# Revit family: d0087280_REVIT-TCX-DUAL
name_source: partatom
category: Mechanical Equipment
revit_build: Autodesk Revit 2017 (Build: 20190507_1515(x64)
units: mm (PartAtom-declared; Revit-internal decimal feet)

## family parameters
Always vertical = Yes
Cut with Voids When Loaded = No
Part Type = Normal
Room Calculation Point = No
Round Connector Dimension = Use Radius
Shared = No
Work Plane-Based = No

## types (44) — shared parameters
Assembly Code = D3040400
Clean in Place Connection NPT = 3/4"
Clean in Place Connection Radius = 3/8"
Controll Access Angle = 45.00°
Description = AquaPLEX® Storage Tank (unlined duplex alloy) with COBREX® Steam Heat Exchanger - Double-wall
Disclaimer = This rendering is for building modeling purposes only. Submittal/catalog is still the contract document. PVI reserves the right to change design and specification without notice.
Drain Angle = 90.00°
Enclosure Height = 16"
Enclosure Width = 8"
From Heater Radius = 1 1/2"
Header Location = 10"
Manufacturer = PVI Industries, LLC
Manway Access Radius = 6 1/2"
Relief NPT = 1"
Relief Radius = 1/2"
Safety Relief Valve NPT = 1"
Safety Relief Valve Radius = 1/2"
Steam Supply Flanged = 3"
To Heater Radius = 1 1/2"
URL = www.pvi.com

## per-type parameters (varying)
- 1200-2 L 250A-TCX: Amps @ 120V=6 A; Cold Inlet Extension=24"; Cold Inlet Height=17 7/8"; Cold Inlet NPT=2"; Cold Inlet Radius=1"; Condensate Connection NPT=1 1/4"; Condensate Connection Radius=5/8"; Drain Extension=26 7/8"; Drain Height=3 1/2"; Drain NPT=1"; Drain Radius=1/2"; Enclosure Extension=30"; Flat Side Distance=45 255/256"; From Heater Extension=24"; From Heater Height=19"; Gallons Storage=250 CF; Height to Enclosure=40"; Hot Outlet NPT=2"; Hot Outlet Radius=1"; Manway Access Extension=26"; Relief Angle=45.00°; Relief Extension=27"; Relief Height=46 1/4"; Skid Length=46"; Skid Spacing=27"; Skid Width Between Centers=31"; TCX=TCX : 1200 150-400; Tank Location=44 77/128"; To Heater Extension=24"; To Heater Height=27"; Unit Diameter=46"; Unit Height=63"; Unit Radius=23"
- 1200-2 L 750A-TCX: Amps @ 120V=6 A; Cold Inlet Extension=34 1/2"; Cold Inlet Height=22 1/2"; Cold Inlet NPT=3"; Cold Inlet Radius=1 1/2"; Condensate Connection NPT=1 1/4"; Condensate Connection Radius=5/8"; Drain Extension=37 3/8"; Drain Height=3 3/4"; Drain NPT=1 1/2"; Drain Radius=3/4"; Enclosure Extension=40 1/2"; Flat Side Distance=66 255/256"; From Heater Extension=34 1/2"; From Heater Height=23"; Gallons Storage=750 CF; Height to Enclosure=54"; Hot Outlet NPT=3"; Hot Outlet Radius=1 1/2"; Manway Access Extension=36 1/2"; Relief Angle=45.00°; Relief Extension=37 1/2"; Relief Height=62 1/4"; Skid Length=68"; Skid Spacing=36"; Skid Width Between Centers=40"; TCX=TCX : 1200 500-1000; Tank Location=55 161/256"; To Heater Extension=34 1/2"; To Heater Height=31"; Unit Diameter=67"; Unit Height=83"; Unit Radius=33 1/2"
- 1200-2 L 900A-TCX: Amps @ 120V=6 A; Cold Inlet Extension=34 1/2"; Cold Inlet Height=22 1/2"; Cold Inlet NPT=3"; Cold Inlet Radius=1 1/2"; Condensate Connection NPT=1 1/4"; Condensate Connection Radius=5/8"; Drain Extension=37 3/8"; Drain Height=3 3/4"; Drain NPT=1 1/2"; Drain Radius=3/4"; Enclosure Extension=40 1/2"; Flat Side Distance=66 255/256"; From Heater Extension=34 1/2"; From Heater Height=23"; Gallons Storage=900 CF; Height to Enclosure=54"; Hot Outlet NPT=3"; Hot Outlet Radius=1 1/2"; Manway Access Extension=36 1/2"; Relief Angle=45.00°; Relief Extension=37 1/2"; Relief Height=74 1/4"; Skid Length=68"; Skid Spacing=36"; Skid Width Between Centers=40"; TCX=TCX : 1200 500-1000; Tank Location=55 161/256"; To Heater Extension=34 1/2"; To Heater Height=31"; Unit Diameter=67"; Unit Height=95"; Unit Radius=33 1/2"
- 1200-2 L 1000A-TCX: Amps @ 120V=6 A; Cold Inlet Extension=34 1/2"; Cold Inlet Height=22 1/2"; Cold Inlet NPT=3"; Cold Inlet Radius=1 1/2"; Condensate Connection NPT=1 1/4"; Condensate Connection Radius=5/8"; Drain Extension=37 3/8"; Drain Height=3 3/4"; Drain NPT=1 1/2"; Drain Radius=3/4"; Enclosure Extension=40 1/2"; Flat Side Distance=66 255/256"; From Heater Extension=34 1/2"; From Heater Height=23"; Gallons Storage=1000 CF; Height to Enclosure=54"; Hot Outlet NPT=3"; Hot Outlet Radius=1 1/2"; Manway Access Extension=36 1/2"; Relief Angle=45.00°; Relief Extension=37 1/2"; Relief Height=86 1/4"; Skid Length=68"; Skid Spacing=36"; Skid Width Between Centers=40"; TCX=TCX : 1200 500-1000; Tank Location=55 161/256"; To Heater Extension=34 1/2"; To Heater Height=31"; Unit Diameter=67"; Unit Height=107"; Unit Radius=33 1/2"
- 1200-2 L 175A-TCX: Amps @ 120V=6 A; Cold Inlet Extension=19 1/2"; Cold Inlet Height=15 3/4"; Cold Inlet NPT=2"; Cold Inlet Radius=1"; Condensate Connection NPT=1 1/4"; Condensate Connection Radius=5/8"; Drain Extension=22 3/8"; Drain Height=3 1/2"; Drain NPT=1"; Drain Radius=1/2"; Enclosure Extension=25 1/2"; Flat Side Distance=34"; From Heater Extension=19 1/2"; From Heater Height=19"; Gallons Storage=175 CF; Height to Enclosure=44"; Hot Outlet NPT=2"; Hot Outlet Radius=1"; Manway Access Extension=1"; Relief Angle=38.00°; Relief Extension=22 1/2"; Relief Height=59 1/4"; Skid Length=37"; Skid Spacing=17"; Skid Width Between Centers=21"; TCX=TCX : 1200 150-400; Tank Location=41 1/4"; To Heater Extension=19 1/2"; To Heater Height=27"; Unit Diameter=37"; Unit Height=71"; Unit Radius=18 1/2"
- 1200-2 L 215A-TCX: Amps @ 120V=6 A; Cold Inlet Extension=19 1/2"; Cold Inlet Height=15 3/4"; Cold Inlet NPT=2"; Cold Inlet Radius=1"; Condensate Connection NPT=1 1/4"; Condensate Connection Radius=5/8"; Drain Extension=22 3/8"; Drain Height=3 1/2"; Drain NPT=1"; Drain Radius=1/2"; Enclosure Extension=25 1/2"; Flat Side Distance=34"; From Heater Extension=19 1/2"; From Heater Height=19"; Gallons Storage=215 CF; Height to Enclosure=54"; Hot Outlet NPT=2"; Hot Outlet Radius=1"; Manway Access Extension=1"; Relief Angle=38.00°; Relief Extension=22 1/2"; Relief Height=66 1/4"; Skid Length=37"; Skid Spacing=17"; Skid Width Between Centers=21"; TCX=TCX : 1200 150-400; Tank Location=41 1/4"; To Heater Extension=19 1/2"; To Heater Height=27"; Unit Diameter=37"; Unit Height=78"; Unit Radius=18 1/2"
- 1800-2 L 150A-TCX: Amps @ 120V=6 A; Cold Inlet Extension=19 1/2"; Cold Inlet Height=15 3/4"; Cold Inlet NPT=2"; Cold Inlet Radius=1"; Condensate Connection NPT=1 1/2"; Condensate Connection Radius=3/4"; Drain Extension=22 3/8"; Drain Height=3 1/2"; Drain NPT=1"; Drain Radius=1/2"; Enclosure Extension=25 1/2"; Flat Side Distance=34"; From Heater Extension=19 1/2"; From Heater Height=19"; Gallons Storage=150 CF; Height to Enclosure=40"; Hot Outlet NPT=2"; Hot Outlet Radius=1"; Manway Access Extension=1"; Relief Angle=38.00°; Relief Extension=22 1/2"; Relief Height=53 1/4"; Skid Length=37"; Skid Spacing=17"; Skid Width Between Centers=21"; TCX=TCX : 1800 150-400; Tank Location=41 1/4"; To Heater Extension=19 1/2"; To Heater Height=27"; Unit Diameter=37"; Unit Height=65"; Unit Radius=18 1/2"
- 1800-2 L 175A-TCX: Amps @ 120V=6 A; Cold Inlet Extension=19 1/2"; Cold Inlet Height=15 3/4"; Cold Inlet NPT=2"; Cold Inlet Radius=1"; Condensate Connection NPT=1 1/2"; Condensate Connection Radius=3/4"; Drain Extension=22 3/8"; Drain Height=3 1/2"; Drain NPT=1"; Drain Radius=1/2"; Enclosure Extension=25 1/2"; Flat Side Distance=34"; From Heater Extension=19 1/2"; From Heater Height=19"; Gallons Storage=175 CF; Height to Enclosure=43"; Hot Outlet NPT=2"; Hot Outlet Radius=1"; Manway Access Extension=1"; Relief Angle=38.00°; Relief Extension=22 1/2"; Relief Height=59 1/4"; Skid Length=37"; Skid Spacing=17"; Skid Width Between Centers=21"; TCX=TCX : 1800 150-400; Tank Location=41 1/4"; To Heater Extension=19 1/2"; To Heater Height=27"; Unit Diameter=37"; Unit Height=71"; Unit Radius=18 1/2"
- 1800-2 L 215A-TCX: Amps @ 120V=6 A; Cold Inlet Extension=19 1/2"; Cold Inlet Height=15 3/4"; Cold Inlet NPT=2"; Cold Inlet Radius=1"; Condensate Connection NPT=1 1/2"; Condensate Connection Radius=3/4"; Drain Extension=22 3/8"; Drain Height=3 1/2"; Drain NPT=1"; Drain Radius=1/2"; Enclosure Extension=25 1/2"; Flat Side Distance=34"; From Heater Extension=19 1/2"; From Heater Height=19"; Gallons Storage=215 CF; Height to Enclosure=54"; Hot Outlet NPT=2"; Hot Outlet Radius=1"; Manway Access Extension=1"; Relief Angle=38.00°; Relief Extension=22 1/2"; Relief Height=66 1/4"; Skid Length=37"; Skid Spacing=17"; Skid Width Between Centers=21"; TCX=TCX : 1800 150-400; Tank Location=41 1/4"; To Heater Extension=19 1/2"; To Heater Height=27"; Unit Diameter=37"; Unit Height=78"; Unit Radius=18 1/2"
- 2700-2 L 150A-TCX: Amps @ 120V=10 A; Cold Inlet Extension=19 1/2"; Cold Inlet Height=15 3/4"; Cold Inlet NPT=2"; Cold Inlet Radius=1"; Condensate Connection NPT=2"; Condensate Connection Radius=1"; Drain Extension=22 3/8"; Drain Height=3 1/2"; Drain NPT=1"; Drain Radius=1/2"; Enclosure Extension=25 1/2"; Flat Side Distance=34"; From Heater Extension=19 1/2"; From Heater Height=19"; Gallons Storage=150 CF; Height to Enclosure=40"; Hot Outlet NPT=2"; Hot Outlet Radius=1"; Manway Access Extension=1"; Relief Angle=38.00°; Relief Extension=22 1/2"; Relief Height=53 1/4"; Skid Length=37"; Skid Spacing=17"; Skid Width Between Centers=21"; TCX=TCX : 2700 150-400; Tank Location=41 1/4"; To Heater Extension=19 1/2"; To Heater Height=27"; Unit Diameter=37"; Unit Height=65"; Unit Radius=18 1/2"
- 2700-2 L 175A-TCX: Amps @ 120V=10 A; Cold Inlet Extension=19 1/2"; Cold Inlet Height=15 3/4"; Cold Inlet NPT=2"; Cold Inlet Radius=1"; Condensate Connection NPT=2"; Condensate Connection Radius=1"; Drain Extension=22 3/8"; Drain Height=3 1/2"; Drain NPT=1"; Drain Radius=1/2"; Enclosure Extension=25 1/2"; Flat Side Distance=34"; From Heater Extension=19 1/2"; From Heater Height=19"; Gallons Storage=175 CF; Height to Enclosure=43"; Hot Outlet NPT=2"; Hot Outlet Radius=1"; Manway Access Extension=1"; Relief Angle=38.00°; Relief Extension=22 1/2"; Relief Height=59 1/4"; Skid Length=37"; Skid Spacing=17"; Skid Width Between Centers=21"; TCX=TCX : 2700 150-400; Tank Location=41 1/4"; To Heater Extension=19 1/2"; To Heater Height=27"; Unit Diameter=37"; Unit Height=71"; Unit Radius=18 1/2"
- 2700-2 L 215A-TCX: Amps @ 120V=10 A; Cold Inlet Extension=19 1/2"; Cold Inlet Height=15 3/4"; Cold Inlet NPT=2"; Cold Inlet Radius=1"; Condensate Connection NPT=2"; Condensate Connection Radius=1"; Drain Extension=22 3/8"; Drain Height=3 1/2"; Drain NPT=1"; Drain Radius=1/2"; Enclosure Extension=25 1/2"; Flat Side Distance=34"; From Heater Extension=19 1/2"; From Heater Height=19"; Gallons Storage=215 CF; Height to Enclosure=54"; Hot Outlet NPT=2"; Hot Outlet Radius=1"; Manway Access Extension=1"; Relief Angle=38.00°; Relief Extension=22 1/2"; Relief Height=66 1/4"; Skid Length=37"; Skid Spacing=17"; Skid Width Between Centers=21"; TCX=TCX : 2700 150-400; Tank Location=41 1/4"; To Heater Extension=19 1/2"; To Heater Height=27"; Unit Diameter=37"; Unit Height=78"; Unit Radius=18 1/2"
- 1200-2 L 300A-TCX: Amps @ 120V=6 A; Cold Inlet Extension=24"; Cold Inlet Height=17 7/8"; Cold Inlet NPT=2"; Cold Inlet Radius=1"; Condensate Connection NPT=1 1/4"; Condensate Connection Radius=5/8"; Drain Extension=26 7/8"; Drain Height=3 1/2"; Drain NPT=1"; Drain Radius=1/2"; Enclosure Extension=30"; Flat Side Distance=45 255/256"; From Heater Extension=24"; From Heater Height=19"; Gallons Storage=300 CF; Height to Enclosure=54"; Hot Outlet NPT=2"; Hot Outlet Radius=1"; Manway Access Extension=26"; Relief Angle=45.00°; Relief Extension=27"; Relief Height=58 1/4"; Skid Length=46"; Skid Spacing=27"; Skid Width Between Centers=31"; TCX=TCX : 1200 150-400; Tank Location=44 77/128"; To Heater Extension=24"; To Heater Height=27"; Unit Diameter=46"; Unit Height=75"; Unit Radius=23"
- 1200-2 L 400A-TCX: Amps @ 120V=6 A; Cold Inlet Extension=24"; Cold Inlet Height=17 7/8"; Cold Inlet NPT=2"; Cold Inlet Radius=1"; Condensate Connection NPT=1 1/4"; Condensate Connection Radius=5/8"; Drain Extension=26 7/8"; Drain Height=3 1/2"; Drain NPT=1"; Drain Radius=1/2"; Enclosure Extension=30"; Flat Side Distance=45 255/256"; From Heater Extension=24"; From Heater Height=19"; Gallons Storage=400 CF; Height to Enclosure=54"; Hot Outlet NPT=2"; Hot Outlet Radius=1"; Manway Access Extension=26"; Relief Angle=45.00°; Relief Extension=27"; Relief Height=70 1/4"; Skid Length=46"; Skid Spacing=27"; Skid Width Between Centers=31"; TCX=TCX : 1200 150-400; Tank Location=44 77/128"; To Heater Extension=24"; To Heater Height=27"; Unit Diameter=46"; Unit Height=87"; Unit Radius=23"
- 1800-2 L 250A-TCX: Amps @ 120V=6 A; Cold Inlet Extension=24"; Cold Inlet Height=17 7/8"; Cold Inlet NPT=2"; Cold Inlet Radius=1"; Condensate Connection NPT=1 1/2"; Condensate Connection Radius=3/4"; Drain Extension=26 7/8"; Drain Height=3 1/2"; Drain NPT=1"; Drain Radius=1/2"; Enclosure Extension=30"; Flat Side Distance=45 255/256"; From Heater Extension=24"; From Heater Height=19"; Gallons Storage=250 CF; Height to Enclosure=40"; Hot Outlet NPT=2"; Hot Outlet Radius=1"; Manway Access Extension=26"; Relief Angle=45.00°; Relief Extension=27"; Relief Height=46 1/4"; Skid Length=46"; Skid Spacing=27"; Skid Width Between Centers=31"; TCX=TCX : 1800 150-400; Tank Location=44 77/128"; To Heater Extension=24"; To Heater Height=27"; Unit Diameter=46"; Unit Height=63"; Unit Radius=23"
- 1800-2 L 300A-TCX: Amps @ 120V=6 A; Cold Inlet Extension=24"; Cold Inlet Height=17 7/8"; Cold Inlet NPT=2"; Cold Inlet Radius=1"; Condensate Connection NPT=1 1/2"; Condensate Connection Radius=3/4"; Drain Extension=26 7/8"; Drain Height=3 1/2"; Drain NPT=1"; Drain Radius=1/2"; Enclosure Extension=30"; Flat Side Distance=45 255/256"; From Heater Extension=24"; From Heater Height=19"; Gallons Storage=300 CF; Height to Enclosure=48"; Hot Outlet NPT=2"; Hot Outlet Radius=1"; Manway Access Extension=26"; Relief Angle=45.00°; Relief Extension=27"; Relief Height=58 1/4"; Skid Length=46"; Skid Spacing=27"; Skid Width Between Centers=31"; TCX=TCX : 1800 150-400; Tank Location=44 77/128"; To Heater Extension=24"; To Heater Height=27"; Unit Diameter=46"; Unit Height=75"; Unit Radius=23"
- 1200-2 L 500A-TCX: Amps @ 120V=6 A; Cold Inlet Extension=29"; Cold Inlet Height=19 3/4"; Cold Inlet NPT=3"; Cold Inlet Radius=1 1/2"; Condensate Connection NPT=1 1/4"; Condensate Connection Radius=5/8"; Drain Extension=31 7/8"; Drain Height=3 3/4"; Drain NPT=1 1/2"; Drain Radius=3/4"; Enclosure Extension=35"; Flat Side Distance=55 255/256"; From Heater Extension=29"; From Heater Height=23"; Gallons Storage=500 CF; Height to Enclosure=54"; Hot Outlet NPT=3"; Hot Outlet Radius=1 1/2"; Manway Access Extension=31"; Relief Angle=45.00°; Relief Extension=32"; Relief Height=59 1/2"; Skid Length=54 1/2"; Skid Spacing=27"; Skid Width Between Centers=31"; TCX=TCX : 1200 500-1000; Tank Location=50 1/8"; To Heater Extension=29"; To Heater Height=31"; Unit Diameter=56"; Unit Height=78"; Unit Radius=28"
- 1200-2 L 600A-TCX: Amps @ 120V=6 A; Cold Inlet Extension=29"; Cold Inlet Height=19 3/4"; Cold Inlet NPT=3"; Cold Inlet Radius=1 1/2"; Condensate Connection NPT=1 1/4"; Condensate Connection Radius=5/8"; Drain Extension=31 7/8"; Drain Height=3 3/4"; Drain NPT=1 1/2"; Drain Radius=3/4"; Enclosure Extension=35"; Flat Side Distance=55 255/256"; From Heater Extension=29"; From Heater Height=23"; Gallons Storage=600 CF; Height to Enclosure=54"; Hot Outlet NPT=3"; Hot Outlet Radius=1 1/2"; Manway Access Extension=31"; Relief Angle=45.00°; Relief Extension=32"; Relief Height=71 1/2"; Skid Length=54 1/2"; Skid Spacing=27"; Skid Width Between Centers=31"; TCX=TCX : 1200 500-1000; Tank Location=50 1/8"; To Heater Extension=29"; To Heater Height=31"; Unit Diameter=56"; Unit Height=90"; Unit Radius=28"
- 1800-2 L 500A-TCX: Amps @ 120V=6 A; Cold Inlet Extension=29"; Cold Inlet Height=19 3/4"; Cold Inlet NPT=3"; Cold Inlet Radius=1 1/2"; Condensate Connection NPT=1 1/2"; Condensate Connection Radius=3/4"; Drain Extension=31 7/8"; Drain Height=3 3/4"; Drain NPT=1 1/2"; Drain Radius=3/4"; Enclosure Extension=35"; Flat Side Distance=55 255/256"; From Heater Extension=29"; From Heater Height=23"; Gallons Storage=500 CF; Height to Enclosure=54"; Hot Outlet NPT=3"; Hot Outlet Radius=1 1/2"; Manway Access Extension=31"; Relief Angle=45.00°; Relief Extension=32"; Relief Height=59 1/2"; Skid Length=54 1/2"; Skid Spacing=27"; Skid Width Between Centers=31"; TCX=TCX : 1800 500-1000; Tank Location=50 1/8"; To Heater Extension=29"; To Heater Height=31"; Unit Diameter=56"; Unit Height=78"; Unit Radius=28"
- 1800-2 L 600A-TCX: Amps @ 120V=6 A; Cold Inlet Extension=29"; Cold Inlet Height=19 3/4"; Cold Inlet NPT=3"; Cold Inlet Radius=1 1/2"; Condensate Connection NPT=1 1/2"; Condensate Connection Radius=3/4"; Drain Extension=31 7/8"; Drain Height=3 3/4"; Drain NPT=1 1/2"; Drain Radius=3/4"; Enclosure Extension=35"; Flat Side Distance=55 255/256"; From Heater Extension=29"; From Heater Height=23"; Gallons Storage=600 CF; Height to Enclosure=54"; Hot Outlet NPT=3"; Hot Outlet Radius=1 1/2"; Manway Access Extension=31"; Relief Angle=45.00°; Relief Extension=32"; Relief Height=71 1/2"; Skid Length=54 1/2"; Skid Spacing=27"; Skid Width Between Centers=31"; TCX=TCX : 1800 500-1000; Tank Location=50 1/8"; To Heater Extension=29"; To Heater Height=31"; Unit Diameter=56"; Unit Height=90"; Unit Radius=28"
- 2700-2 L 500A-TCX: Amps @ 120V=10 A; Cold Inlet Extension=29"; Cold Inlet Height=19 3/4"; Cold Inlet NPT=3"; Cold Inlet Radius=1 1/2"; Condensate Connection NPT=2"; Condensate Connection Radius=1"; Drain Extension=31 7/8"; Drain Height=3 3/4"; Drain NPT=1 1/2"; Drain Radius=3/4"; Enclosure Extension=35"; Flat Side Distance=55 255/256"; From Heater Extension=29"; From Heater Height=23"; Gallons Storage=500 CF; Height to Enclosure=54"; Hot Outlet NPT=3"; Hot Outlet Radius=1 1/2"; Manway Access Extension=31"; Relief Angle=38.00°; Relief Extension=32"; Relief Height=59 1/2"; Skid Length=54 1/2"; Skid Spacing=27"; Skid Width Between Centers=31"; TCX=TCX : 2700 500-1000; Tank Location=50 1/8"; To Heater Extension=29"; To Heater Height=31"; Unit Diameter=56"; Unit Height=78"; Unit Radius=28"
- 2700-2 L 600A-TCX: Amps @ 120V=10 A; Cold Inlet Extension=29"; Cold Inlet Height=19 3/4"; Cold Inlet NPT=3"; Cold Inlet Radius=1 1/2"; Condensate Connection NPT=2"; Condensate Connection Radius=1"; Drain Extension=31 7/8"; Drain Height=3 3/4"; Drain NPT=1 1/2"; Drain Radius=3/4"; Enclosure Extension=35"; Flat Side Distance=55 255/256"; From Heater Extension=29"; From Heater Height=23"; Gallons Storage=600 CF; Height to Enclosure=54"; Hot Outlet NPT=3"; Hot Outlet Radius=1 1/2"; Manway Access Extension=31"; Relief Angle=38.00°; Relief Extension=32"; Relief Height=71 1/2"; Skid Length=54 1/2"; Skid Spacing=27"; Skid Width Between Centers=31"; TCX=TCX : 2700 500-1000; Tank Location=50 1/8"; To Heater Extension=29"; To Heater Height=31"; Unit Diameter=56"; Unit Height=90"; Unit Radius=28"
- 3600-2 L 500A-TCX: Amps @ 120V=10 A; Cold Inlet Extension=29"; Cold Inlet Height=19 3/4"; Cold Inlet NPT=3"; Cold Inlet Radius=1 1/2"; Condensate Connection NPT=2"; Condensate Connection Radius=1"; Drain Extension=31 7/8"; Drain Height=3 3/4"; Drain NPT=1 1/2"; Drain Radius=3/4"; Enclosure Extension=35"; Flat Side Distance=55 255/256"; From Heater Extension=29"; From Heater Height=23"; Gallons Storage=500 CF; Height to Enclosure=54"; Hot Outlet NPT=3"; Hot Outlet Radius=1 1/2"; Manway Access Extension=31"; Relief Angle=45.00°; Relief Extension=32"; Relief Height=59 1/2"; Skid Length=54 1/2"; Skid Spacing=27"; Skid Width Between Centers=31"; TCX=TCX : 3600 500-1000; Tank Location=50 1/8"; To Heater Extension=29"; To Heater Height=31"; Unit Diameter=56"; Unit Height=78"; Unit Radius=28"
- 3600-2 L 600A-TCX: Amps @ 120V=10 A; Cold Inlet Extension=29"; Cold Inlet Height=19 3/4"; Cold Inlet NPT=3"; Cold Inlet Radius=1 1/2"; Condensate Connection NPT=2"; Condensate Connection Radius=1"; Drain Extension=31 7/8"; Drain Height=3 3/4"; Drain NPT=1 1/2"; Drain Radius=3/4"; Enclosure Extension=35"; Flat Side Distance=55 255/256"; From Heater Extension=29"; From Heater Height=23"; Gallons Storage=600 CF; Height to Enclosure=54"; Hot Outlet NPT=3"; Hot Outlet Radius=1 1/2"; Manway Access Extension=31"; Relief Angle=45.00°; Relief Extension=32"; Relief Height=71 1/2"; Skid Length=54 1/2"; Skid Spacing=27"; Skid Width Between Centers=31"; TCX=TCX : 3600 500-1000; Tank Location=50 1/8"; To Heater Extension=29"; To Heater Height=31"; Unit Diameter=56"; Unit Height=90"; Unit Radius=28"
- 3600-2 L 150A-TCX: Amps @ 120V=10 A; Cold Inlet Extension=19 1/2"; Cold Inlet Height=15 3/4"; Cold Inlet NPT=2"; Cold Inlet Radius=1"; Condensate Connection NPT=2"; Condensate Connection Radius=1"; Drain Extension=22 3/8"; Drain Height=3 1/2"; Drain NPT=1"; Drain Radius=1/2"; Enclosure Extension=25 1/2"; Flat Side Distance=34"; From Heater Extension=19 1/2"; From Heater Height=19"; Gallons Storage=150 CF; Height to Enclosure=40"; Hot Outlet NPT=2"; Hot Outlet Radius=1"; Manway Access Extension=1"; Relief Angle=38.00°; Relief Extension=22 1/2"; Relief Height=53 1/4"; Skid Length=37"; Skid Spacing=17"; Skid Width Between Centers=21"; TCX=TCX : 3600 150-400; Tank Location=41 1/4"; To Heater Extension=19 1/2"; To Heater Height=27"; Unit Diameter=37"; Unit Height=65"; Unit Radius=18 1/2"
- 3600-2 L 175A-TCX: Amps @ 120V=10 A; Cold Inlet Extension=19 1/2"; Cold Inlet Height=15 3/4"; Cold Inlet NPT=2"; Cold Inlet Radius=1"; Condensate Connection NPT=2"; Condensate Connection Radius=1"; Drain Extension=22 3/8"; Drain Height=3 1/2"; Drain NPT=1"; Drain Radius=1/2"; Enclosure Extension=25 1/2"; Flat Side Distance=34"; From Heater Extension=19 1/2"; From Heater Height=19"; Gallons Storage=175 CF; Height to Enclosure=43"; Hot Outlet NPT=2"; Hot Outlet Radius=1"; Manway Access Extension=1"; Relief Angle=38.00°; Relief Extension=22 1/2"; Relief Height=59 1/4"; Skid Length=37"; Skid Spacing=17"; Skid Width Between Centers=21"; TCX=TCX : 3600 150-400; Tank Location=41 1/4"; To Heater Extension=19 1/2"; To Heater Height=27"; Unit Diameter=37"; Unit Height=71"; Unit Radius=18 1/2"
- 3600-2 L 215A-TCX: Amps @ 120V=10 A; Cold Inlet Extension=19 1/2"; Cold Inlet Height=15 3/4"; Cold Inlet NPT=2"; Cold Inlet Radius=1"; Condensate Connection NPT=2"; Condensate Connection Radius=1"; Drain Extension=22 3/8"; Drain Height=3 1/2"; Drain NPT=1"; Drain Radius=1/2"; Enclosure Extension=25 1/2"; Flat Side Distance=34"; From Heater Extension=19 1/2"; From Heater Height=19"; Gallons Storage=215 CF; Height to Enclosure=54"; Hot Outlet NPT=2"; Hot Outlet Radius=1"; Manway Access Extension=1"; Relief Angle=38.00°; Relief Extension=22 1/2"; Relief Height=66 1/4"; Skid Length=37"; Skid Spacing=17"; Skid Width Between Centers=21"; TCX=TCX : 3600 150-400; Tank Location=41 1/4"; To Heater Extension=19 1/2"; To Heater Height=27"; Unit Diameter=37"; Unit Height=78"; Unit Radius=18 1/2"
- 1800-2 L 400A-TCX: Amps @ 120V=6 A; Cold Inlet Extension=24"; Cold Inlet Height=17 7/8"; Cold Inlet NPT=2"; Cold Inlet Radius=1"; Condensate Connection NPT=1 1/2"; Condensate Connection Radius=3/4"; Drain Extension=26 7/8"; Drain Height=3 1/2"; Drain NPT=1"; Drain Radius=1/2"; Enclosure Extension=30"; Flat Side Distance=45 255/256"; From Heater Extension=24"; From Heater Height=19"; Gallons Storage=400 CF; Height to Enclosure=54"; Hot Outlet NPT=2"; Hot Outlet Radius=1"; Manway Access Extension=26"; Relief Angle=45.00°; Relief Extension=27"; Relief Height=70 1/4"; Skid Length=46"; Skid Spacing=27"; Skid Width Between Centers=31"; TCX=TCX : 1800 150-400; Tank Location=44 77/128"; To Heater Extension=24"; To Heater Height=27"; Unit Diameter=46"; Unit Height=87"; Unit Radius=23"
- 2700-2 L 250A-TCX: Amps @ 120V=10 A; Cold Inlet Extension=24"; Cold Inlet Height=17 7/8"; Cold Inlet NPT=2"; Cold Inlet Radius=1"; Condensate Connection NPT=2"; Condensate Connection Radius=1"; Drain Extension=26 7/8"; Drain Height=3 1/2"; Drain NPT=1"; Drain Radius=1/2"; Enclosure Extension=30"; Flat Side Distance=45 255/256"; From Heater Extension=24"; From Heater Height=19"; Gallons Storage=250 CF; Height to Enclosure=40"; Hot Outlet NPT=2"; Hot Outlet Radius=1"; Manway Access Extension=26"; Relief Angle=45.00°; Relief Extension=27"; Relief Height=46 1/4"; Skid Length=46"; Skid Spacing=27"; Skid Width Between Centers=31"; TCX=TCX : 2700 150-400; Tank Location=44 77/128"; To Heater Extension=24"; To Heater Height=27"; Unit Diameter=46"; Unit Height=63"; Unit Radius=23"
- 2700-2 L 300A-TCX: Amps @ 120V=10 A; Cold Inlet Extension=24"; Cold Inlet Height=17 7/8"; Cold Inlet NPT=2"; Cold Inlet Radius=1"; Condensate Connection NPT=2"; Condensate Connection Radius=1"; Drain Extension=26 7/8"; Drain Height=3 1/2"; Drain NPT=1"; Drain Radius=1/2"; Enclosure Extension=30"; Flat Side Distance=45 255/256"; From Heater Extension=24"; From Heater Height=19"; Gallons Storage=300 CF; Height to Enclosure=48"; Hot Outlet NPT=2"; Hot Outlet Radius=1"; Manway Access Extension=26"; Relief Angle=45.00°; Relief Extension=27"; Relief Height=58 1/4"; Skid Length=46"; Skid Spacing=27"; Skid Width Between Centers=31"; TCX=TCX : 2700 150-400; Tank Location=44 77/128"; To Heater Extension=24"; To Heater Height=27"; Unit Diameter=46"; Unit Height=75"; Unit Radius=23"
- 2700-2 L 400A-TCX: Amps @ 120V=10 A; Cold Inlet Extension=24"; Cold Inlet Height=17 7/8"; Cold Inlet NPT=2"; Cold Inlet Radius=1"; Condensate Connection NPT=2"; Condensate Connection Radius=1"; Drain Extension=26 7/8"; Drain Height=3 1/2"; Drain NPT=1"; Drain Radius=1/2"; Enclosure Extension=30"; Flat Side Distance=45 255/256"; From Heater Extension=24"; From Heater Height=19"; Gallons Storage=400 CF; Height to Enclosure=54"; Hot Outlet NPT=2"; Hot Outlet Radius=1"; Manway Access Extension=26"; Relief Angle=45.00°; Relief Extension=27"; Relief Height=70 1/4"; Skid Length=46"; Skid Spacing=27"; Skid Width Between Centers=31"; TCX=TCX : 2700 150-400; Tank Location=44 77/128"; To Heater Extension=24"; To Heater Height=27"; Unit Diameter=46"; Unit Height=87"; Unit Radius=23"
- 3600-2 L 250A-TCX: Amps @ 120V=10 A; Cold Inlet Extension=24"; Cold Inlet Height=17 7/8"; Cold Inlet NPT=2"; Cold Inlet Radius=1"; Condensate Connection NPT=2"; Condensate Connection Radius=1"; Drain Extension=26 7/8"; Drain Height=3 1/2"; Drain NPT=1"; Drain Radius=1/2"; Enclosure Extension=30"; Flat Side Distance=45 255/256"; From Heater Extension=24"; From Heater Height=19"; Gallons Storage=250 CF; Height to Enclosure=40"; Hot Outlet NPT=2"; Hot Outlet Radius=1"; Manway Access Extension=26"; Relief Angle=45.00°; Relief Extension=27"; Relief Height=46 1/4"; Skid Length=46"; Skid Spacing=27"; Skid Width Between Centers=31"; TCX=TCX : 3600 150-400; Tank Location=44 77/128"; To Heater Extension=24"; To Heater Height=27"; Unit Diameter=46"; Unit Height=63"; Unit Radius=23"
- 3600-2 L 300A-TCX: Amps @ 120V=10 A; Cold Inlet Extension=24"; Cold Inlet Height=17 7/8"; Cold Inlet NPT=2"; Cold Inlet Radius=1"; Condensate Connection NPT=2"; Condensate Connection Radius=1"; Drain Extension=26 7/8"; Drain Height=3 1/2"; Drain NPT=1"; Drain Radius=1/2"; Enclosure Extension=30"; Flat Side Distance=45 255/256"; From Heater Extension=24"; From Heater Height=19"; Gallons Storage=300 CF; Height to Enclosure=48"; Hot Outlet NPT=2"; Hot Outlet Radius=1"; Manway Access Extension=26"; Relief Angle=45.00°; Relief Extension=27"; Relief Height=58 1/4"; Skid Length=46"; Skid Spacing=27"; Skid Width Between Centers=31"; TCX=TCX : 3600 150-400; Tank Location=44 77/128"; To Heater Extension=24"; To Heater Height=27"; Unit Diameter=46"; Unit Height=75"; Unit Radius=23"
- 3600-2 L 400A-TCX: Amps @ 120V=10 A; Cold Inlet Extension=24"; Cold Inlet Height=17 7/8"; Cold Inlet NPT=2"; Cold Inlet Radius=1"; Condensate Connection NPT=2"; Condensate Connection Radius=1"; Drain Extension=26 7/8"; Drain Height=3 1/2"; Drain NPT=1"; Drain Radius=1/2"; Enclosure Extension=30"; Flat Side Distance=45 255/256"; From Heater Extension=24"; From Heater Height=19"; Gallons Storage=400 CF; Height to Enclosure=54"; Hot Outlet NPT=2"; Hot Outlet Radius=1"; Manway Access Extension=26"; Relief Angle=45.00°; Relief Extension=27"; Relief Height=70 1/4"; Skid Length=46"; Skid Spacing=27"; Skid Width Between Centers=31"; TCX=TCX : 3600 150-400; Tank Location=44 77/128"; To Heater Extension=24"; To Heater Height=27"; Unit Diameter=46"; Unit Height=87"; Unit Radius=23"
- 1800-2 L 750A-TCX: Amps @ 120V=6 A; Cold Inlet Extension=34 1/2"; Cold Inlet Height=22 1/2"; Cold Inlet NPT=3"; Cold Inlet Radius=1 1/2"; Condensate Connection NPT=1 1/2"; Condensate Connection Radius=3/4"; Drain Extension=37 3/8"; Drain Height=3 3/4"; Drain NPT=1 1/2"; Drain Radius=3/4"; Enclosure Extension=40 1/2"; Flat Side Distance=66 255/256"; From Heater Extension=34 1/2"; From Heater Height=23"; Gallons Storage=750 CF; Height to Enclosure=54"; Hot Outlet NPT=3"; Hot Outlet Radius=1 1/2"; Manway Access Extension=36 1/2"; Relief Angle=45.00°; Relief Extension=37 1/2"; Relief Height=62 1/4"; Skid Length=68"; Skid Spacing=36"; Skid Width Between Centers=40"; TCX=TCX : 1800 500-1000; Tank Location=55 161/256"; To Heater Extension=34 1/2"; To Heater Height=31"; Unit Diameter=67"; Unit Height=83"; Unit Radius=33 1/2"
- 2700-2 L 750A-TCX: Amps @ 120V=10 A; Cold Inlet Extension=34 1/2"; Cold Inlet Height=22 1/2"; Cold Inlet NPT=3"; Cold Inlet Radius=1 1/2"; Condensate Connection NPT=2"; Condensate Connection Radius=1"; Drain Extension=37 3/8"; Drain Height=3 3/4"; Drain NPT=1 1/2"; Drain Radius=3/4"; Enclosure Extension=40 1/2"; Flat Side Distance=66 255/256"; From Heater Extension=34 1/2"; From Heater Height=23"; Gallons Storage=750 CF; Height to Enclosure=54"; Hot Outlet NPT=3"; Hot Outlet Radius=1 1/2"; Manway Access Extension=36 1/2"; Relief Angle=45.00°; Relief Extension=37 1/2"; Relief Height=62 1/4"; Skid Length=68"; Skid Spacing=36"; Skid Width Between Centers=40"; TCX=TCX : 2700 500-1000; Tank Location=55 161/256"; To Heater Extension=34 1/2"; To Heater Height=31"; Unit Diameter=67"; Unit Height=83"; Unit Radius=33 1/2"
- 3600-2 L 750A-TCX: Amps @ 120V=10 A; Cold Inlet Extension=34 1/2"; Cold Inlet Height=22 1/2"; Cold Inlet NPT=3"; Cold Inlet Radius=1 1/2"; Condensate Connection NPT=2"; Condensate Connection Radius=1"; Drain Extension=37 3/8"; Drain Height=3 3/4"; Drain NPT=1 1/2"; Drain Radius=3/4"; Enclosure Extension=40 1/2"; Flat Side Distance=66 255/256"; From Heater Extension=34 1/2"; From Heater Height=23"; Gallons Storage=750 CF; Height to Enclosure=54"; Hot Outlet NPT=3"; Hot Outlet Radius=1 1/2"; Manway Access Extension=36 1/2"; Relief Angle=45.00°; Relief Extension=37 1/2"; Relief Height=62 1/4"; Skid Length=68"; Skid Spacing=36"; Skid Width Between Centers=40"; TCX=TCX : 3600 500-1000; Tank Location=55 161/256"; To Heater Extension=34 1/2"; To Heater Height=31"; Unit Diameter=67"; Unit Height=83"; Unit Radius=33 1/2"
- 1800-2 L 900A-TCX: Amps @ 120V=6 A; Cold Inlet Extension=34 1/2"; Cold Inlet Height=22 1/2"; Cold Inlet NPT=3"; Cold Inlet Radius=1 1/2"; Condensate Connection NPT=1 1/2"; Condensate Connection Radius=3/4"; Drain Extension=37 3/8"; Drain Height=3 3/4"; Drain NPT=1 1/2"; Drain Radius=3/4"; Enclosure Extension=40 1/2"; Flat Side Distance=66 255/256"; From Heater Extension=34 1/2"; From Heater Height=23"; Gallons Storage=900 CF; Height to Enclosure=54"; Hot Outlet NPT=3"; Hot Outlet Radius=1 1/2"; Manway Access Extension=36 1/2"; Relief Angle=45.00°; Relief Extension=37 1/2"; Relief Height=74 1/4"; Skid Length=68"; Skid Spacing=36"; Skid Width Between Centers=40"; TCX=TCX : 1800 500-1000; Tank Location=55 161/256"; To Heater Extension=34 1/2"; To Heater Height=31"; Unit Diameter=67"; Unit Height=95"; Unit Radius=33 1/2"
- 2700-2 L 900A-TCX: Amps @ 120V=10 A; Cold Inlet Extension=34 1/2"; Cold Inlet Height=22 1/2"; Cold Inlet NPT=3"; Cold Inlet Radius=1 1/2"; Condensate Connection NPT=2"; Condensate Connection Radius=1"; Drain Extension=37 3/8"; Drain Height=3 3/4"; Drain NPT=1 1/2"; Drain Radius=3/4"; Enclosure Extension=40 1/2"; Flat Side Distance=66 255/256"; From Heater Extension=34 1/2"; From Heater Height=23"; Gallons Storage=900 CF; Height to Enclosure=54"; Hot Outlet NPT=3"; Hot Outlet Radius=1 1/2"; Manway Access Extension=36 1/2"; Relief Angle=45.00°; Relief Extension=37 1/2"; Relief Height=74 1/4"; Skid Length=68"; Skid Spacing=36"; Skid Width Between Centers=40"; TCX=TCX : 2700 500-1000; Tank Location=55 161/256"; To Heater Extension=34 1/2"; To Heater Height=31"; Unit Diameter=67"; Unit Height=95"; Unit Radius=33 1/2"
- 3600-2 L 900A-TCX: Amps @ 120V=10 A; Cold Inlet Extension=34 1/2"; Cold Inlet Height=22 1/2"; Cold Inlet NPT=3"; Cold Inlet Radius=1 1/2"; Condensate Connection NPT=2"; Condensate Connection Radius=1"; Drain Extension=37 3/8"; Drain Height=3 3/4"; Drain NPT=1 1/2"; Drain Radius=3/4"; Enclosure Extension=40 1/2"; Flat Side Distance=66 255/256"; From Heater Extension=34 1/2"; From Heater Height=23"; Gallons Storage=900 CF; Height to Enclosure=54"; Hot Outlet NPT=3"; Hot Outlet Radius=1 1/2"; Manway Access Extension=36 1/2"; Relief Angle=45.00°; Relief Extension=37 1/2"; Relief Height=74 1/4"; Skid Length=68"; Skid Spacing=36"; Skid Width Between Centers=40"; TCX=TCX : 3600 500-1000; Tank Location=55 161/256"; To Heater Extension=34 1/2"; To Heater Height=31"; Unit Diameter=67"; Unit Height=95"; Unit Radius=33 1/2"
- 1800-2 L 1000A-TCX: Amps @ 120V=6 A; Cold Inlet Extension=34 1/2"; Cold Inlet Height=22 1/2"; Cold Inlet NPT=3"; Cold Inlet Radius=1 1/2"; Condensate Connection NPT=1 1/2"; Condensate Connection Radius=3/4"; Drain Extension=37 3/8"; Drain Height=3 3/4"; Drain NPT=1 1/2"; Drain Radius=3/4"; Enclosure Extension=40 1/2"; Flat Side Distance=66 255/256"; From Heater Extension=34 1/2"; From Heater Height=23"; Gallons Storage=1000 CF; Height to Enclosure=54"; Hot Outlet NPT=3"; Hot Outlet Radius=1 1/2"; Manway Access Extension=36 1/2"; Relief Angle=45.00°; Relief Extension=37 1/2"; Relief Height=86 1/4"; Skid Length=68"; Skid Spacing=36"; Skid Width Between Centers=40"; TCX=TCX : 1800 500-1000; Tank Location=55 161/256"; To Heater Extension=34 1/2"; To Heater Height=31"; Unit Diameter=67"; Unit Height=107"; Unit Radius=33 1/2"
- 2700-2 L 1000A-TCX: Amps @ 120V=10 A; Cold Inlet Extension=34 1/2"; Cold Inlet Height=22 1/2"; Cold Inlet NPT=3"; Cold Inlet Radius=1 1/2"; Condensate Connection NPT=2"; Condensate Connection Radius=1"; Drain Extension=37 3/8"; Drain Height=3 3/4"; Drain NPT=1 1/2"; Drain Radius=3/4"; Enclosure Extension=40 1/2"; Flat Side Distance=66 255/256"; From Heater Extension=34 1/2"; From Heater Height=23"; Gallons Storage=1000 CF; Height to Enclosure=54"; Hot Outlet NPT=3"; Hot Outlet Radius=1 1/2"; Manway Access Extension=36 1/2"; Relief Angle=45.00°; Relief Extension=37 1/2"; Relief Height=86 1/4"; Skid Length=68"; Skid Spacing=36"; Skid Width Between Centers=40"; TCX=TCX : 2700 500-1000; Tank Location=55 161/256"; To Heater Extension=34 1/2"; To Heater Height=31"; Unit Diameter=67"; Unit Height=107"; Unit Radius=33 1/2"
- 3600-2 L 1000A-TCX: Amps @ 120V=10 A; Cold Inlet Extension=34 1/2"; Cold Inlet Height=22 1/2"; Cold Inlet NPT=3"; Cold Inlet Radius=1 1/2"; Condensate Connection NPT=2"; Condensate Connection Radius=1"; Drain Extension=37 3/8"; Drain Height=3 3/4"; Drain NPT=1 1/2"; Drain Radius=3/4"; Enclosure Extension=40 1/2"; Flat Side Distance=66 255/256"; From Heater Extension=34 1/2"; From Heater Height=23"; Gallons Storage=1000 CF; Height to Enclosure=54"; Hot Outlet NPT=3"; Hot Outlet Radius=1 1/2"; Manway Access Extension=36 1/2"; Relief Angle=45.00°; Relief Extension=37 1/2"; Relief Height=86 1/4"; Skid Length=68"; Skid Spacing=36"; Skid Width Between Centers=40"; TCX=TCX : 3600 500-1000; Tank Location=55 161/256"; To Heater Extension=34 1/2"; To Heater Height=31"; Unit Diameter=67"; Unit Height=107"; Unit Radius=33 1/2"
- 1200-2 L 150A-TCX: Amps @ 120V=6 A; Cold Inlet Extension=19 1/2"; Cold Inlet Height=15 3/4"; Cold Inlet NPT=2"; Cold Inlet Radius=1"; Condensate Connection NPT=1 1/4"; Condensate Connection Radius=5/8"; Drain Extension=22 3/8"; Drain Height=3 1/2"; Drain NPT=1"; Drain Radius=1/2"; Enclosure Extension=25 1/2"; Flat Side Distance=34"; From Heater Extension=19 1/2"; From Heater Height=19"; Gallons Storage=150 CF; Height to Enclosure=40"; Hot Outlet NPT=2"; Hot Outlet Radius=1"; Manway Access Extension=1"; Relief Angle=38.00°; Relief Extension=22 1/2"; Relief Height=53 1/4"; Skid Length=37"; Skid Spacing=17"; Skid Width Between Centers=21"; TCX=TCX : 1200 150-400; Tank Location=41 1/4"; To Heater Extension=19 1/2"; To Heater Height=27"; Unit Diameter=37"; Unit Height=65"; Unit Radius=18 1/2"

note: column(s) folded — value = type name in every type: Model

## geometry (parser evidence)
native form markers: Sweep x5
no freeform markers — native parametric forms only
